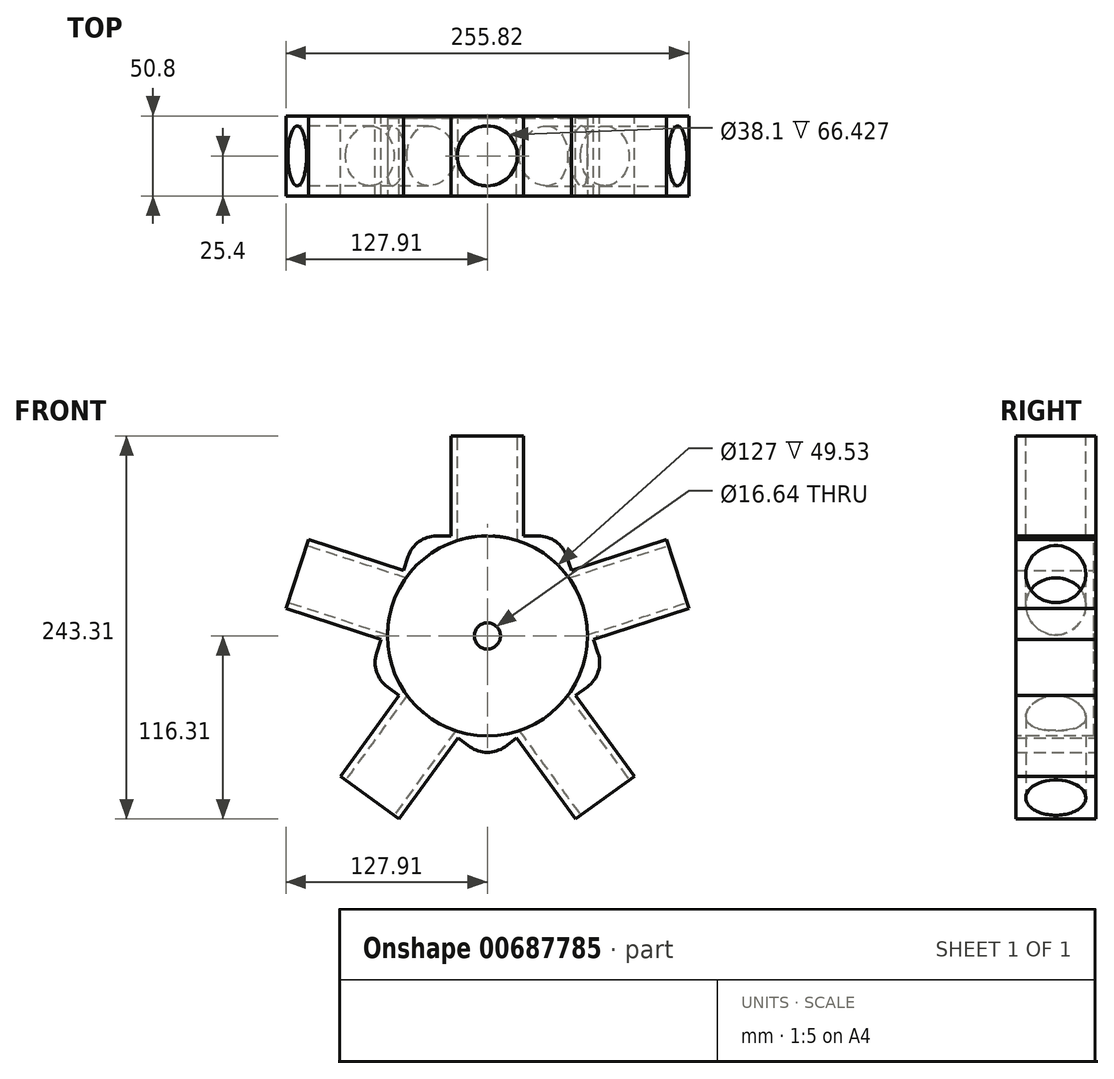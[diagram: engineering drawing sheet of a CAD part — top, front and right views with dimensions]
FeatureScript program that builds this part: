
annotation { "Feature Type Name" : "Feature", "Feature Type Description" : "" }
export const myFeature = defineFeature(function(context is Context, id is Id, definition is map)
    precondition{}
    {
        {
            var Q0;
            Q0=qCreatedBy(makeId("Front.planeOp"),FACE);
            var sketch = newSketch(context, id + "F0", { "sketchPlane" : qUnion([Q0])});
            skPoint(sketch, "E0.middle", {"position": v(0, 63.5) * mm});
            skPoint(sketch, "E1.center", {"position": v(-0.27, 0.15) * mm});
            skLineSegment(sketch, "E2.bottom", {"start": v(33.4, -54) * mm, "end": v(32.38, -54) * mm});
            skLineSegment(sketch, "E2.top", {"start": v(62.79, -9.5) * mm, "end": v(62.25, -9.5) * mm});
            skPoint(sketch, "E2.left.end.orphan", {"position": v(117.96, -9.5) * mm});
            skLineSegment(sketch, "E3.0", {"start": v(-46.14, 63.5) * mm, "end": v(-23.07, 63.5) * mm});
            skLineSegment(sketch, "E3.1", {"start": v(46.14, 63.5) * mm, "end": v(53.26, 41.56) * mm});
            skLineSegment(sketch, "E3.2", {"start": v(74.65, -24.25) * mm, "end": v(56, -37.81) * mm});
            skLineSegment(sketch, "E3.3", {"start": v(0, -78.5) * mm, "end": v(-18.66, -64.93) * mm});
            skLineSegment(sketch, "E3.4", {"start": v(-74.65, -24.25) * mm, "end": v(-67.52, -2.32) * mm});
            skPoint(sketch, "E4", {"position": v(53.26, 41.56) * mm});
            skPoint(sketch, "E5", {"position": v(67.52, -2.32) * mm});
            skLineSegment(sketch, "E6", {"start": v(53.26, 41.56) * mm, "end": v(113.66, 61.18) * mm});
            skLineSegment(sketch, "E7", {"start": v(67.52, -2.32) * mm, "end": v(127.91, 17.3) * mm});
            skLineSegment(sketch, "E8", {"start": v(127.91, 17.3) * mm, "end": v(113.66, 61.18) * mm});
            skPoint(sketch, "E9", {"position": v(-23.07, 63.5) * mm});
            skPoint(sketch, "E10", {"position": v(23.07, 63.5) * mm});
            skLineSegment(sketch, "E11", {"start": v(-23.07, 63.5) * mm, "end": v(-23.07, 127) * mm});
            skLineSegment(sketch, "E12", {"start": v(23.07, 63.5) * mm, "end": v(23.07, 127) * mm});
            skLineSegment(sketch, "E13", {"start": v(23.07, 127) * mm, "end": v(-23.07, 127) * mm});
            skPoint(sketch, "E14", {"position": v(-53.26, 41.57) * mm});
            skPoint(sketch, "E15", {"position": v(-67.52, -2.32) * mm});
            skPoint(sketch, "E16", {"position": v(-56, -37.81) * mm});
            skPoint(sketch, "E17", {"position": v(-18.66, -64.93) * mm});
            skPoint(sketch, "E18", {"position": v(18.66, -64.93) * mm});
            skPoint(sketch, "E19", {"position": v(56, -37.81) * mm});
            skLineSegment(sketch, "E20", {"start": v(-53.26, 41.57) * mm, "end": v(-113.65, 61.19) * mm});
            skLineSegment(sketch, "E21", {"start": v(-113.65, 61.19) * mm, "end": v(-127.9, 17.32) * mm});
            skLineSegment(sketch, "E22", {"start": v(-127.9, 17.32) * mm, "end": v(-67.52, -2.32) * mm});
            skLineSegment(sketch, "E23", {"start": v(-56, -37.81) * mm, "end": v(-93.31, -89.18) * mm});
            skLineSegment(sketch, "E24", {"start": v(-18.66, -64.93) * mm, "end": v(-55.98, -116.3) * mm});
            skLineSegment(sketch, "E25", {"start": v(-55.98, -116.3) * mm, "end": v(-93.31, -89.18) * mm});
            skLineSegment(sketch, "E26", {"start": v(18.66, -64.93) * mm, "end": v(55.98, -116.3) * mm});
            skLineSegment(sketch, "E27", {"start": v(55.98, -116.3) * mm, "end": v(93.3, -89.2) * mm});
            skLineSegment(sketch, "E28", {"start": v(56, -37.81) * mm, "end": v(93.3, -89.2) * mm});
            skArc(sketch, "E29.trimOffspring", {"start": v(33.4, -54) * mm, "mid": v(35.4, -52.72) * mm, "end": v(37.32, -51.37) * mm});
            skLineSegment(sketch, "E30.trimOffspring", {"start": v(-56, -37.81) * mm, "end": v(-74.65, -24.25) * mm});
            skLineSegment(sketch, "E31.trimOffspring", {"start": v(23.07, 63.5) * mm, "end": v(46.14, 63.5) * mm});
            skLineSegment(sketch, "E32.trimOffspring", {"start": v(-53.26, 41.57) * mm, "end": v(-46.14, 63.5) * mm});
            skLineSegment(sketch, "E33.trimOffspring", {"start": v(18.66, -64.93) * mm, "end": v(0, -78.5) * mm});
            skLineSegment(sketch, "E34.trimOffspring", {"start": v(67.52, -2.32) * mm, "end": v(74.65, -24.25) * mm});
            skSolve(sketch);
        }
        {
            var Q0;
            {var subQ20=sQuery(id+"F0.wireOp",EDGE,"E30.trimOffspring");Q0=makeQuery(id+"F0.imprint","IMPRINT",FACE,{"disambiguationData":[TD([[makeQuery(id+"F0.imprint","IMPRINT",EDGE,{"derivedFrom":subQ20}),-1.0]])]});}
            var Q1;
            {var subQ0=sQuery(id+"F0.wireOp",EDGE,"E6");Q1=makeQuery(id+"F0.imprint","IMPRINT",FACE,{"disambiguationData":[TD([[makeQuery(id+"F0.imprint","IMPRINT",EDGE,{"derivedFrom":subQ0}),-1.0]])]});}
            var Q2;
            {var subQ2=sQuery(id+"F0.wireOp",EDGE,"E1.1.1");Q2=makeQuery(id+"F0.imprint","IMPRINT",FACE,{"disambiguationData":[TD([[makeQuery(id+"F0.imprint","IMPRINT",EDGE,{"derivedFrom":subQ2}),-1.0]])]});}
            var Q3;
            {var subQ3=sQuery(id+"F0.wireOp",EDGE,"E20");Q3=makeQuery(id+"F0.imprint","IMPRINT",FACE,{"disambiguationData":[TD([[makeQuery(id+"F0.imprint","IMPRINT",EDGE,{"derivedFrom":subQ3}),1.0]])]});}
            var Q4;
            Q4=makeQuery(id+"F0.imprint","IMPRINT",FACE,{"disambiguationData":[TD([[makeQuery(id+"F0.imprint","IMPRINT",EDGE,{"derivedFrom":sQuery(id+"F0.wireOp",EDGE,"E23")}),1.0]])]});
            var Q5;
            {var subQ0=sQuery(id+"F0.wireOp",EDGE,"E26");Q5=makeQuery(id+"F0.imprint","IMPRINT",FACE,{"disambiguationData":[TD([[makeQuery(id+"F0.imprint","IMPRINT",EDGE,{"derivedFrom":subQ0}),1.0]])]});}
            extrude(context, id + "F1", {"entities" : qUnion([Q0, Q1, Q2, Q3, Q4, Q5]), "depth" : 50.8 * mm, "offsetDistance" : 25.4 * mm});
        }
        {
            var Q0;
            Q0=makeQuery(id+"F1.opExtrude","CAP_FACE",FACE,{"disambiguationData":[OSD([sQuery(id+"F0.wireOp",EDGE,"E3.0"),sQuery(id+"F0.wireOp",EDGE,"E3.1"),sQuery(id+"F0.wireOp",EDGE,"E3.2"),sQuery(id+"F0.wireOp",EDGE,"E3.3"),sQuery(id+"F0.wireOp",EDGE,"E3.4"),sQuery(id+"F0.wireOp",EDGE,"E6"),sQuery(id+"F0.wireOp",EDGE,"E7"),sQuery(id+"F0.wireOp",EDGE,"E8"),sQuery(id+"F0.wireOp",EDGE,"E11"),sQuery(id+"F0.wireOp",EDGE,"E12"),sQuery(id+"F0.wireOp",EDGE,"E13"),sQuery(id+"F0.wireOp",EDGE,"E20"),sQuery(id+"F0.wireOp",EDGE,"E21"),sQuery(id+"F0.wireOp",EDGE,"E22"),sQuery(id+"F0.wireOp",EDGE,"E23"),sQuery(id+"F0.wireOp",EDGE,"E24"),sQuery(id+"F0.wireOp",EDGE,"E25"),sQuery(id+"F0.wireOp",EDGE,"E26"),sQuery(id+"F0.wireOp",EDGE,"E27"),sQuery(id+"F0.wireOp",EDGE,"E28"),sQuery(id+"F0.wireOp",EDGE,"517dc5cb-3545-4ec9-9af4-f299af5a043f.trimOffspring"),sQuery(id+"F0.wireOp",EDGE,"E30.trimOffspring"),sQuery(id+"F0.wireOp",EDGE,"E31.trimOffspring")])],"isStart":false});
            var sketch = newSketch(context, id + "F2", { "sketchPlane" : qUnion([Q0])});
            skCircle(sketch, "E35", {"center": v(0, 0) * mm, "radius": 63.5 * mm});
            skSolve(sketch);
        }
        {
            var Q0;
            Q0=makeQuery(id+"F2.imprint","IMPRINT",FACE,{"disambiguationData":[TD([[makeQuery(id+"F2.imprint","IMPRINT",EDGE,{"derivedFrom":sQuery(id+"F2.wireOp",EDGE,"E35")}),1.0]])]});
            extrude(context, id + "F3", {"entities" : qUnion([Q0]), "operationType" : NewBodyOperationType.REMOVE, "oppositeDirection" : true, "depth" : 49.53 * mm, "offsetDistance" : 25.4 * mm});
        }
        {
            var Q0;
            Q0=makeQuery(id+"F1.opExtrude","CAP_FACE",FACE,{"disambiguationData":[OSD([sQuery(id+"F0.wireOp",EDGE,"E3.0"),sQuery(id+"F0.wireOp",EDGE,"E3.1"),sQuery(id+"F0.wireOp",EDGE,"E3.2"),sQuery(id+"F0.wireOp",EDGE,"E3.3"),sQuery(id+"F0.wireOp",EDGE,"E3.4"),sQuery(id+"F0.wireOp",EDGE,"E6"),sQuery(id+"F0.wireOp",EDGE,"E7"),sQuery(id+"F0.wireOp",EDGE,"E8"),sQuery(id+"F0.wireOp",EDGE,"E11"),sQuery(id+"F0.wireOp",EDGE,"E12"),sQuery(id+"F0.wireOp",EDGE,"E13"),sQuery(id+"F0.wireOp",EDGE,"E20"),sQuery(id+"F0.wireOp",EDGE,"E21"),sQuery(id+"F0.wireOp",EDGE,"E22"),sQuery(id+"F0.wireOp",EDGE,"E23"),sQuery(id+"F0.wireOp",EDGE,"E24"),sQuery(id+"F0.wireOp",EDGE,"E25"),sQuery(id+"F0.wireOp",EDGE,"E26"),sQuery(id+"F0.wireOp",EDGE,"E27"),sQuery(id+"F0.wireOp",EDGE,"E28"),sQuery(id+"F0.wireOp",EDGE,"E30.trimOffspring"),sQuery(id+"F0.wireOp",EDGE,"E31.trimOffspring"),sQuery(id+"F0.wireOp",EDGE,"E32.trimOffspring"),sQuery(id+"F0.wireOp",EDGE,"E33.trimOffspring"),sQuery(id+"F0.wireOp",EDGE,"E34.trimOffspring")])],"isStart":true});
            var sketch = newSketch(context, id + "F4", { "sketchPlane" : qUnion([Q0])});
            skCircle(sketch, "E36", {"center": v(0, 0) * mm, "radius": 8.32 * mm});
            skSolve(sketch);
        }
        {
            var Q0;
            Q0=makeQuery(id+"F4.imprint","IMPRINT",FACE,{"disambiguationData":[TD([[makeQuery(id+"F4.imprint","IMPRINT",EDGE,{"derivedFrom":sQuery(id+"F4.wireOp",EDGE,"E36")}),1.0]])]});
            extrude(context, id + "F5", {"entities" : qUnion([Q0]), "operationType" : NewBodyOperationType.REMOVE, "oppositeDirection" : true, "depth" : 25.4 * mm, "offsetDistance" : 25.4 * mm});
        }
        {
            var Q0;
            Q0=makeQuery(id+"F1.opExtrude","SWEPT_FACE",FACE,{"disambiguationData":[OSD([sQuery(id+"F0.wireOp",EDGE,"E13")])]});
            var sketch = newSketch(context, id + "F6", { "sketchPlane" : qUnion([Q0])});
            skCircle(sketch, "E37", {"center": v(0, -25.4) * mm, "radius": 19.05 * mm});
            skPoint(sketch, "E37.centerSnap0", {"position": v(23.07, -25.4) * mm});
            skSolve(sketch);
        }
        {
            var Q0;
            Q0=makeQuery(id+"F1.opExtrude","SWEPT_FACE",FACE,{"disambiguationData":[OSD([sQuery(id+"F0.wireOp",EDGE,"E8")])]});
            var sketch = newSketch(context, id + "F7", { "sketchPlane" : qUnion([Q0])});
            skCircle(sketch, "E38", {"center": v(-25.4, 0) * mm, "radius": 19.05 * mm});
            skPoint(sketch, "E38.centerSnap0", {"position": v(-25.4, -23.07) * mm});
            skSolve(sketch);
        }
        {
            var Q0;
            Q0=makeQuery(id+"F1.opExtrude","SWEPT_FACE",FACE,{"disambiguationData":[OSD([sQuery(id+"F0.wireOp",EDGE,"E27")])]});
            var sketch = newSketch(context, id + "F8", { "sketchPlane" : qUnion([Q0])});
            skCircle(sketch, "E39", {"center": v(0, 25.4) * mm, "radius": 19.05 * mm});
            skPoint(sketch, "E39.centerSnap0", {"position": v(-23.07, 25.4) * mm});
            skSolve(sketch);
        }
        {
            var Q0;
            Q0=makeQuery(id+"F1.opExtrude","SWEPT_FACE",FACE,{"disambiguationData":[OSD([sQuery(id+"F0.wireOp",EDGE,"E25")])]});
            var sketch = newSketch(context, id + "F9", { "sketchPlane" : qUnion([Q0])});
            skCircle(sketch, "E40", {"center": v(0, 25.4) * mm, "radius": 19.05 * mm});
            skPoint(sketch, "E40.centerSnap0", {"position": v(-23.07, 25.4) * mm});
            skSolve(sketch);
        }
        {
            var Q0;
            Q0=makeQuery(id+"F1.opExtrude","SWEPT_FACE",FACE,{"disambiguationData":[OSD([sQuery(id+"F0.wireOp",EDGE,"E21")])]});
            var sketch = newSketch(context, id + "F10", { "sketchPlane" : qUnion([Q0])});
            skCircle(sketch, "E41", {"center": v(25.4, 0) * mm, "radius": 19.05 * mm});
            skPoint(sketch, "E41.centerSnap0", {"position": v(25.4, 23.07) * mm});
            skSolve(sketch);
        }
        {
            var Q0;
            Q0=makeQuery(id+"F9.imprint","IMPRINT",FACE,{"disambiguationData":[TD([[makeQuery(id+"F9.imprint","IMPRINT",EDGE,{"derivedFrom":sQuery(id+"F9.wireOp",EDGE,"E40")}),1.0]])]});
            extrude(context, id + "F11", {"entities" : qUnion([Q0]), "operationType" : NewBodyOperationType.REMOVE, "oppositeDirection" : true, "depth" : 76.2 * mm, "offsetDistance" : 25.4 * mm});
        }
        {
            var Q0;
            Q0=makeQuery(id+"F10.imprint","IMPRINT",FACE,{"disambiguationData":[TD([[makeQuery(id+"F10.imprint","IMPRINT",EDGE,{"derivedFrom":sQuery(id+"F10.wireOp",EDGE,"E41")}),1.0]])]});
            extrude(context, id + "F12", {"entities" : qUnion([Q0]), "operationType" : NewBodyOperationType.REMOVE, "oppositeDirection" : true, "depth" : 76.2 * mm, "offsetDistance" : 25.4 * mm});
        }
        {
            var Q0;
            Q0=makeQuery(id+"F6.imprint","IMPRINT",FACE,{"disambiguationData":[TD([[makeQuery(id+"F6.imprint","IMPRINT",EDGE,{"derivedFrom":sQuery(id+"F6.wireOp",EDGE,"E37")}),1.0]])]});
            extrude(context, id + "F13", {"entities" : qUnion([Q0]), "operationType" : NewBodyOperationType.REMOVE, "oppositeDirection" : true, "depth" : 76.2 * mm, "offsetDistance" : 25.4 * mm});
        }
        {
            var Q0;
            Q0=makeQuery(id+"F7.imprint","IMPRINT",FACE,{"disambiguationData":[TD([[makeQuery(id+"F7.imprint","IMPRINT",EDGE,{"derivedFrom":sQuery(id+"F7.wireOp",EDGE,"E38")}),1.0]])]});
            extrude(context, id + "F14", {"entities" : qUnion([Q0]), "operationType" : NewBodyOperationType.REMOVE, "oppositeDirection" : true, "depth" : 76.2 * mm, "offsetDistance" : 25.4 * mm});
        }
        {
            var Q0;
            Q0=makeQuery(id+"F8.imprint","IMPRINT",FACE,{"disambiguationData":[TD([[makeQuery(id+"F8.imprint","IMPRINT",EDGE,{"derivedFrom":sQuery(id+"F8.wireOp",EDGE,"E39")}),1.0]])]});
            extrude(context, id + "F15", {"entities" : qUnion([Q0]), "operationType" : NewBodyOperationType.REMOVE, "oppositeDirection" : true, "depth" : 76.2 * mm, "offsetDistance" : 25.4 * mm});
        }
        {
            var Q0;
            Q0=makeQuery(id+"F1.opExtrude","SWEPT_EDGE",EDGE,{"disambiguationData":[OSD([sQuery(id+"F0.wireOp",EDGE,"E3.3"),sQuery(id+"F0.wireOp",EDGE,"E33.trimOffspring")])]});
            var Q1;
            Q1=makeQuery(id+"F1.opExtrude","SWEPT_EDGE",EDGE,{"disambiguationData":[OSD([sQuery(id+"F0.wireOp",EDGE,"E3.2"),sQuery(id+"F0.wireOp",EDGE,"E34.trimOffspring")])]});
            var Q2;
            Q2=makeQuery(id+"F1.opExtrude","SWEPT_EDGE",EDGE,{"disambiguationData":[OSD([sQuery(id+"F0.wireOp",EDGE,"E3.4"),sQuery(id+"F0.wireOp",EDGE,"E30.trimOffspring")])]});
            var Q3;
            Q3=makeQuery(id+"F1.opExtrude","SWEPT_EDGE",EDGE,{"disambiguationData":[OSD([sQuery(id+"F0.wireOp",EDGE,"E3.0"),sQuery(id+"F0.wireOp",EDGE,"E32.trimOffspring")])]});
            var Q4;
            Q4=makeQuery(id+"F1.opExtrude","SWEPT_EDGE",EDGE,{"disambiguationData":[OSD([sQuery(id+"F0.wireOp",EDGE,"E3.1"),sQuery(id+"F0.wireOp",EDGE,"E31.trimOffspring")])]});
            fillet(context, id + "F16", {"entities" : qUnion([Q0, Q1, Q2, Q3, Q4]), "radius" : 19.05 * mm, "tangentPropagation" : true, "allowEdgeOverflow" : false});
        }
    });
